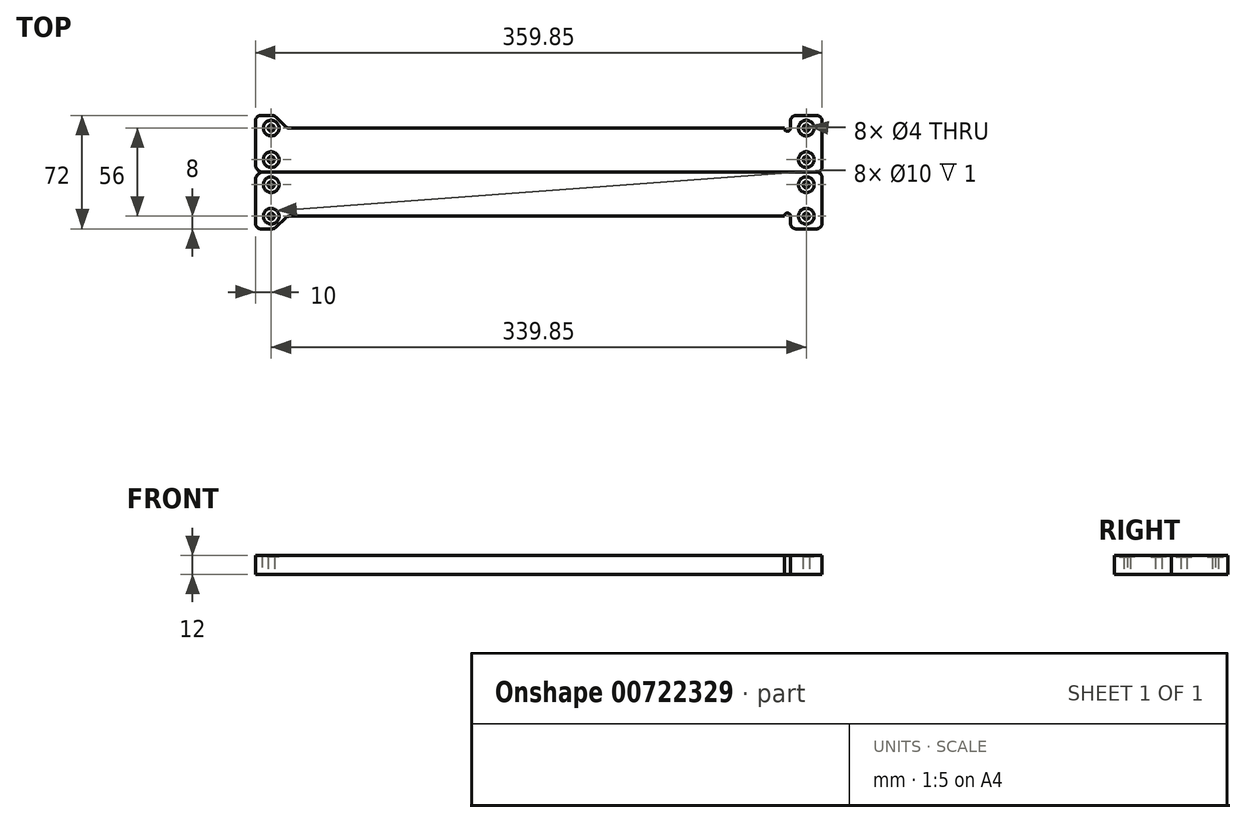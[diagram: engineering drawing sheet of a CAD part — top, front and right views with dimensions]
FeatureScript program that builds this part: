
annotation { "Feature Type Name" : "Feature", "Feature Type Description" : "" }
export const myFeature = defineFeature(function(context is Context, id is Id, definition is map)
    precondition{}
    {
        {
            var Q0;
            Q0=qCreatedBy(makeId("Top.planeOp"),FACE);
            var sketch = newSketch(context, id + "F0", { "sketchPlane" : qUnion([Q0])});
            skLineSegment(sketch, "E0", {"start": v(0, 0) * mm, "end": v(0, 28) * mm, "construction": true});
            skLineSegment(sketch, "E1", {"start": v(1.4, 28) * mm, "end": v(315.85, 28) * mm});
            skLineSegment(sketch, "E2", {"start": v(319.85, 28) * mm, "end": v(319.85, 32.6) * mm});
            skLineSegment(sketch, "E3", {"start": v(323.25, 36) * mm, "end": v(336.45, 36) * mm});
            skLineSegment(sketch, "E4", {"start": v(339.85, 32.6) * mm, "end": v(339.85, 3.4) * mm});
            skLineSegment(sketch, "E5", {"start": v(336.45, 0) * mm, "end": v(329.85, 0) * mm});
            skLineSegment(sketch, "E6", {"start": v(-1, 29) * mm, "end": v(-7, 35) * mm});
            skLineSegment(sketch, "E7", {"start": v(-9.4, 36) * mm, "end": v(-16.6, 36) * mm});
            skLineSegment(sketch, "E8", {"start": v(-20, 32.6) * mm, "end": v(-20, 4.95) * mm});
            skLineSegment(sketch, "E9", {"start": v(-10, 36) * mm, "end": v(-10, 0) * mm, "construction": true});
            skCircle(sketch, "E10", {"center": v(-10, 28) * mm, "radius": 2 * mm});
            skCircle(sketch, "E11", {"center": v(-10, 8) * mm, "radius": 2 * mm});
            skCircle(sketch, "E12", {"center": v(-10, 28) * mm, "radius": 5 * mm});
            skCircle(sketch, "E13", {"center": v(-10, 8) * mm, "radius": 5 * mm});
            skLineSegment(sketch, "E14", {"start": v(329.85, 36) * mm, "end": v(329.85, 0) * mm, "construction": true});
            skCircle(sketch, "E15", {"center": v(329.85, 8) * mm, "radius": 2 * mm});
            skCircle(sketch, "E16", {"center": v(329.85, 28) * mm, "radius": 2 * mm});
            skCircle(sketch, "E17", {"center": v(329.85, 28) * mm, "radius": 5 * mm});
            skCircle(sketch, "E18", {"center": v(329.85, 8) * mm, "radius": 5 * mm});
            skPoint(sketch, "E19.visualSharp", {"position": v(319.85, 36) * mm});
            skArc(sketch, "E19.filletArc", {"start": v(323.25, 36) * mm, "mid": v(320.85, 35) * mm, "end": v(319.85, 32.6) * mm});
            skPoint(sketch, "E20.visualSharp", {"position": v(339.85, 36) * mm});
            skArc(sketch, "E20.filletArc", {"start": v(339.85, 32.6) * mm, "mid": v(338.85, 35) * mm, "end": v(336.45, 36) * mm});
            skPoint(sketch, "E21.visualSharp", {"position": v(339.85, 0) * mm});
            skArc(sketch, "E21.filletArc", {"start": v(336.45, 0) * mm, "mid": v(338.85, 1) * mm, "end": v(339.85, 3.4) * mm});
            skPoint(sketch, "E22.visualSharp", {"position": v(-8, 36) * mm});
            skArc(sketch, "E22.filletArc", {"start": v(-7, 35) * mm, "mid": v(-8.1, 35.74) * mm, "end": v(-9.4, 36) * mm});
            skPoint(sketch, "E23.visualSharp", {"position": v(-20, 36) * mm});
            skArc(sketch, "E23.filletArc", {"start": v(-16.6, 36) * mm, "mid": v(-19, 35) * mm, "end": v(-20, 32.6) * mm});
            skPoint(sketch, "E24.visualSharp", {"position": v(-20, 0) * mm});
            skPoint(sketch, "E25.visualSharp", {"position": v(0, 28) * mm});
            skArc(sketch, "E25.filletArc", {"start": v(-1, 29) * mm, "mid": v(0.1, 28.26) * mm, "end": v(1.4, 28) * mm});
            skLineSegment(sketch, "E26", {"start": v(329.85, 0) * mm, "end": v(0, 0) * mm});
            skArc(sketch, "E27.filletArc", {"start": v(-20, 4.95) * mm, "mid": v(-18.78, 1.68) * mm, "end": v(-15.73, 0) * mm});
            skLineSegment(sketch, "E28", {"start": v(0, -16.1) * mm, "end": v(215.82, -16.1) * mm, "construction": true});
            skLineSegment(sketch, "E29", {"start": v(-15.73, 0) * mm, "end": v(0, 0) * mm});
            skArc(sketch, "E30", {"start": v(315.85, 28) * mm, "mid": v(317.85, 26) * mm, "end": v(319.85, 28) * mm});
            skSolve(sketch);
        }
        {
            var Q0;
            Q0 = qSketchRegion(id + "F0", true);
            var Q1;
            Q1=makeQuery(id+"F0.imprint","IMPRINT",FACE,{"disambiguationData":[TD([[makeQuery(id+"F0.imprint","IMPRINT",EDGE,{"derivedFrom":sQuery(id+"F0.wireOp",EDGE,"E10")}),-1.0]])]});
            var Q2;
            Q2=makeQuery(id+"F0.imprint","IMPRINT",FACE,{"disambiguationData":[TD([[makeQuery(id+"F0.imprint","IMPRINT",EDGE,{"derivedFrom":sQuery(id+"F0.wireOp",EDGE,"E11")}),-1.0]])]});
            var Q3;
            Q3=makeQuery(id+"F0.imprint","IMPRINT",FACE,{"disambiguationData":[TD([[makeQuery(id+"F0.imprint","IMPRINT",EDGE,{"derivedFrom":sQuery(id+"F0.wireOp",EDGE,"E15")}),-1.0]])]});
            var Q4;
            Q4=makeQuery(id+"F0.imprint","IMPRINT",FACE,{"disambiguationData":[TD([[makeQuery(id+"F0.imprint","IMPRINT",EDGE,{"derivedFrom":sQuery(id+"F0.wireOp",EDGE,"E16")}),-1.0]])]});
            extrude(context, id + "F1", {"entities" : qUnion([Q0, Q1, Q2, Q3, Q4]), "depth" : 12 * mm, "offsetDistance" : 25 * mm});
        }
        {
            var Q0;
            Q0=makeQuery(id+"F1.opExtrude","CAP_FACE",FACE,{"disambiguationData":[OSD([sQuery(id+"F0.wireOp",EDGE,"E1"),sQuery(id+"F0.wireOp",EDGE,"E2"),sQuery(id+"F0.wireOp",EDGE,"E3"),sQuery(id+"F0.wireOp",EDGE,"E4"),sQuery(id+"F0.wireOp",EDGE,"E5"),sQuery(id+"F0.wireOp",EDGE,"E6"),sQuery(id+"F0.wireOp",EDGE,"E7"),sQuery(id+"F0.wireOp",EDGE,"E8"),sQuery(id+"F0.wireOp",EDGE,"QT8f5H8D-H1RM-RT4f-ZX45-cuhHGmmUbyoB"),sQuery(id+"F0.wireOp",EDGE,"E10"),sQuery(id+"F0.wireOp",EDGE,"E11"),sQuery(id+"F0.wireOp",EDGE,"E15"),sQuery(id+"F0.wireOp",EDGE,"E16"),sQuery(id+"F0.wireOp",EDGE,"Bn4uxYnR-SQf1-61sf-YCne-iKvvS3XxUmHH"),sQuery(id+"F0.wireOp",EDGE,"uqFojYeH-vqTm-8Ebw-r5c4-WReHswfoVIg7"),sQuery(id+"F0.wireOp",EDGE,"tDERgD4x-kfIV-ukeN-kEXs-4P2PNLj4bWF2"),sQuery(id+"F0.wireOp",EDGE,"E19.filletArc"),sQuery(id+"F0.wireOp",EDGE,"ce69405e-0037-4598-8867-19b88ac9c4f8.filletArc"),sQuery(id+"F0.wireOp",EDGE,"0f29e9b5-fa7c-4275-8907-7fbf71b27cb1.filletArc"),sQuery(id+"F0.wireOp",EDGE,"E20.filletArc"),sQuery(id+"F0.wireOp",EDGE,"E21.filletArc"),sQuery(id+"F0.wireOp",EDGE,"E22.filletArc"),sQuery(id+"F0.wireOp",EDGE,"E23.filletArc"),sQuery(id+"F0.wireOp",EDGE,"E24.filletArc"),sQuery(id+"F0.wireOp",EDGE,"E25.filletArc")])],"isStart":false});
            var sketch = newSketch(context, id + "F2", { "sketchPlane" : qUnion([Q0])});
            skCircle(sketch, "E31.0", {"center": v(329.85, 28) * mm, "radius": 5 * mm});
            skCircle(sketch, "E32.0", {"center": v(329.85, 8) * mm, "radius": 5 * mm});
            skCircle(sketch, "E33.0", {"center": v(-10, 8) * mm, "radius": 5 * mm});
            skCircle(sketch, "E34.0", {"center": v(-10, 28) * mm, "radius": 5 * mm});
            skSolve(sketch);
        }
        {
            var Q0;
            Q0 = qSketchRegion(id + "F2", true);
            extrude(context, id + "F3", {"entities" : qUnion([Q0]), "operationType" : NewBodyOperationType.REMOVE, "oppositeDirection" : true, "depth" : 1 * mm, "offsetDistance" : 25 * mm});
        }
        {
            var Q0;
            Q0=makeQuery(id+"F1.opExtrude","CAP_FACE",FACE,{"disambiguationData":[OSD([sQuery(id+"F0.wireOp",EDGE,"E1"),sQuery(id+"F0.wireOp",EDGE,"E2"),sQuery(id+"F0.wireOp",EDGE,"E3"),sQuery(id+"F0.wireOp",EDGE,"E4"),sQuery(id+"F0.wireOp",EDGE,"E5"),sQuery(id+"F0.wireOp",EDGE,"E6"),sQuery(id+"F0.wireOp",EDGE,"E7"),sQuery(id+"F0.wireOp",EDGE,"E8"),sQuery(id+"F0.wireOp",EDGE,"QT8f5H8D-H1RM-RT4f-ZX45-cuhHGmmUbyoB"),sQuery(id+"F0.wireOp",EDGE,"E12"),sQuery(id+"F0.wireOp",EDGE,"E13"),sQuery(id+"F0.wireOp",EDGE,"E17"),sQuery(id+"F0.wireOp",EDGE,"E18"),sQuery(id+"F0.wireOp",EDGE,"Bn4uxYnR-SQf1-61sf-YCne-iKvvS3XxUmHH"),sQuery(id+"F0.wireOp",EDGE,"uqFojYeH-vqTm-8Ebw-r5c4-WReHswfoVIg7"),sQuery(id+"F0.wireOp",EDGE,"tDERgD4x-kfIV-ukeN-kEXs-4P2PNLj4bWF2"),sQuery(id+"F0.wireOp",EDGE,"E19.filletArc"),sQuery(id+"F0.wireOp",EDGE,"ce69405e-0037-4598-8867-19b88ac9c4f8.filletArc"),sQuery(id+"F0.wireOp",EDGE,"0f29e9b5-fa7c-4275-8907-7fbf71b27cb1.filletArc"),sQuery(id+"F0.wireOp",EDGE,"E20.filletArc"),sQuery(id+"F0.wireOp",EDGE,"E21.filletArc"),sQuery(id+"F0.wireOp",EDGE,"E22.filletArc"),sQuery(id+"F0.wireOp",EDGE,"E23.filletArc"),sQuery(id+"F0.wireOp",EDGE,"E24.filletArc"),sQuery(id+"F0.wireOp",EDGE,"E25.filletArc")])],"isStart":false});
            var sketch = newSketch(context, id + "F4", { "sketchPlane" : qUnion([Q0])});
            skLineSegment(sketch, "E35", {"start": v(6.93, 22.63) * mm, "end": v(6.93, 12.63) * mm});
            skArc(sketch, "E36.0.startCap", {"start": v(5.23, 22.63) * mm, "mid": v(6.93, 24.33) * mm, "end": v(8.63, 22.63) * mm});
            skArc(sketch, "E36.0.endCap", {"start": v(8.63, 12.63) * mm, "mid": v(6.93, 10.93) * mm, "end": v(5.23, 12.63) * mm});
            skLineSegment(sketch, "E36.0.left", {"start": v(8.63, 22.63) * mm, "end": v(8.63, 12.63) * mm});
            skLineSegment(sketch, "E36.0.right", {"start": v(5.23, 22.63) * mm, "end": v(5.23, 12.63) * mm});
            skArc(sketch, "E37.1.0.0", {"start": v(11.23, 22.63) * mm, "mid": v(12.93, 24.33) * mm, "end": v(14.63, 22.63) * mm});
            skLineSegment(sketch, "E37.1.0.1", {"start": v(11.23, 22.63) * mm, "end": v(11.23, 12.63) * mm});
            skLineSegment(sketch, "E37.1.0.2", {"start": v(14.63, 22.63) * mm, "end": v(14.63, 12.63) * mm});
            skArc(sketch, "E37.1.0.3", {"start": v(14.63, 12.63) * mm, "mid": v(12.93, 10.93) * mm, "end": v(11.23, 12.63) * mm});
            skLineSegment(sketch, "E37.direction1", {"start": v(5.23, 22.63) * mm, "end": v(11.23, 22.63) * mm, "construction": true});
            skSolve(sketch);
        }
        {
            var Q0;
            Q0=makeQuery(id+"F1.opExtrude","SWEPT_BODY",BODY,{"disambiguationData":[OSD([sQuery(id+"F0.wireOp",EDGE,"E1"),sQuery(id+"F0.wireOp",EDGE,"E2"),sQuery(id+"F0.wireOp",EDGE,"E3"),sQuery(id+"F0.wireOp",EDGE,"E4"),sQuery(id+"F0.wireOp",EDGE,"E5"),sQuery(id+"F0.wireOp",EDGE,"E6"),sQuery(id+"F0.wireOp",EDGE,"E7"),sQuery(id+"F0.wireOp",EDGE,"E8"),sQuery(id+"F0.wireOp",EDGE,"E10"),sQuery(id+"F0.wireOp",EDGE,"E11"),sQuery(id+"F0.wireOp",EDGE,"E15"),sQuery(id+"F0.wireOp",EDGE,"E16"),sQuery(id+"F0.wireOp",EDGE,"Bn4uxYnR-SQf1-61sf-YCne-iKvvS3XxUmHH"),sQuery(id+"F0.wireOp",EDGE,"uqFojYeH-vqTm-8Ebw-r5c4-WReHswfoVIg7"),sQuery(id+"F0.wireOp",EDGE,"tDERgD4x-kfIV-ukeN-kEXs-4P2PNLj4bWF2"),sQuery(id+"F0.wireOp",EDGE,"E19.filletArc"),sQuery(id+"F0.wireOp",EDGE,"ce69405e-0037-4598-8867-19b88ac9c4f8.filletArc"),sQuery(id+"F0.wireOp",EDGE,"0f29e9b5-fa7c-4275-8907-7fbf71b27cb1.filletArc"),sQuery(id+"F0.wireOp",EDGE,"E20.filletArc"),sQuery(id+"F0.wireOp",EDGE,"E21.filletArc"),sQuery(id+"F0.wireOp",EDGE,"E22.filletArc"),sQuery(id+"F0.wireOp",EDGE,"E23.filletArc"),sQuery(id+"F0.wireOp",EDGE,"E25.filletArc"),sQuery(id+"F0.wireOp",EDGE,"be8dcd3a-d1c8-49eb-a2e1-593493788622"),sQuery(id+"F0.wireOp",EDGE,"E27.filletArc")])]});
            var Q1;
            Q1=qCreatedBy(makeId("Front.planeOp"),FACE);
            mirror(context, id + "F5", {"entities" : qUnion([Q0]), "mirrorPlane" : qUnion([Q1])});
        }
    });
